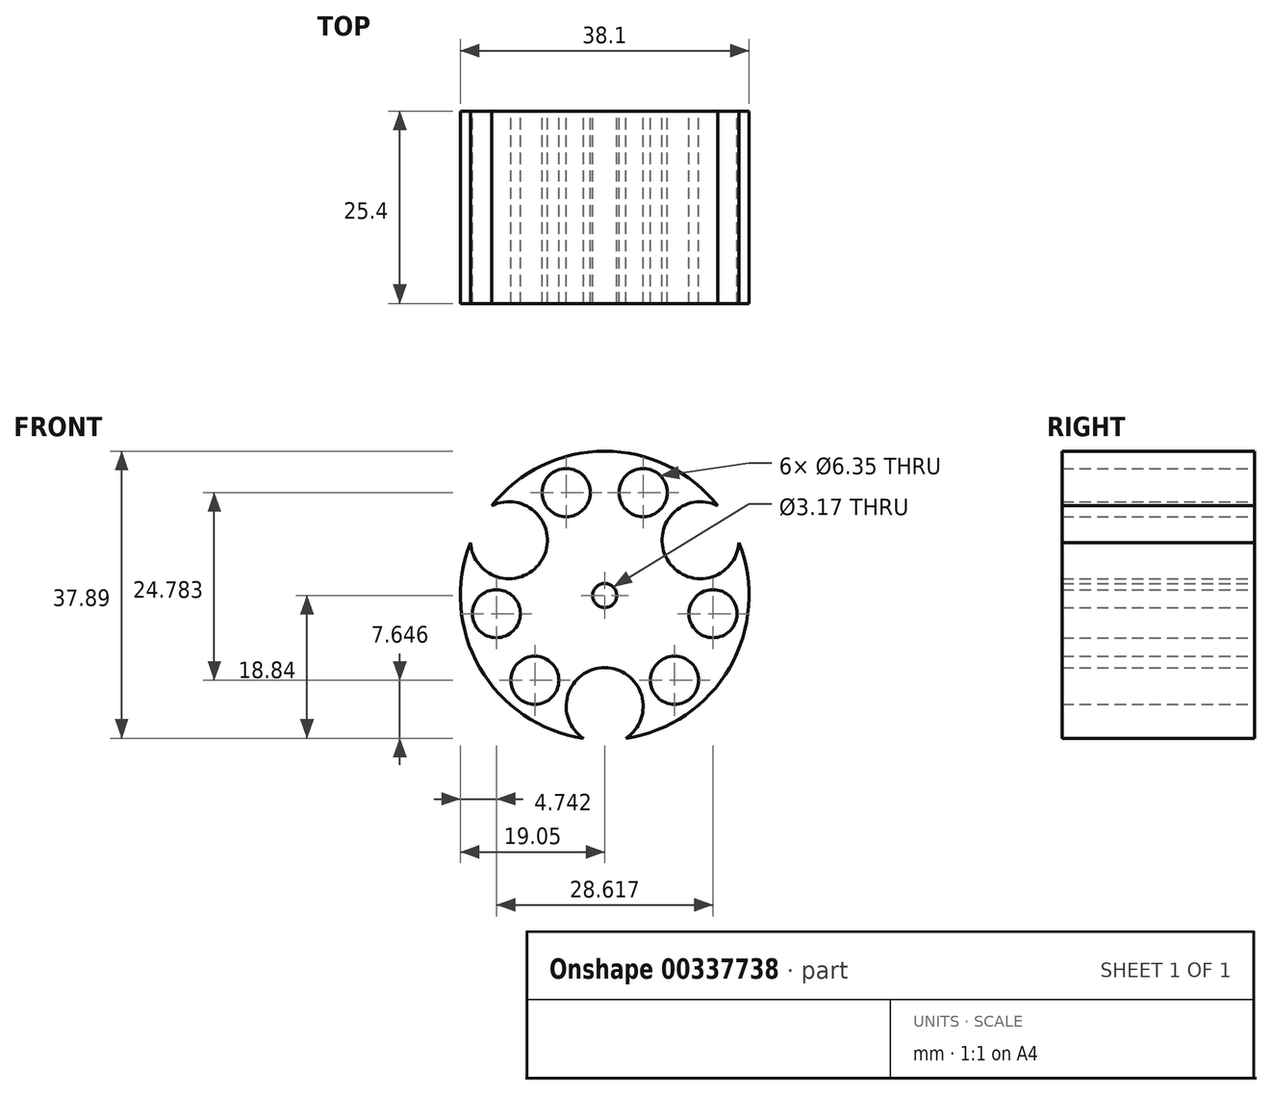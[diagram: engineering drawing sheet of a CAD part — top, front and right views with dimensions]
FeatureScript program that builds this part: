
annotation { "Feature Type Name" : "Feature", "Feature Type Description" : "" }
export const myFeature = defineFeature(function(context is Context, id is Id, definition is map)
    precondition{}
    {
        {
            var Q0;
            Q0=qCreatedBy(makeId("Front.planeOp"),FACE);
            var sketch = newSketch(context, id + "F0", { "sketchPlane" : qUnion([Q0])});
            skCircle(sketch, "E0", {"center": v(0, 0) * mm, "radius": 19.05 * mm, "construction": true});
            skCircle(sketch, "E1.cCircle", {"center": v(0, 0) * mm, "radius": 9.53 * mm, "construction": true});
            skPoint(sketch, "E2", {"position": v(0, -19.05) * mm});
            skPoint(sketch, "E3", {"position": v(-16.5, 9.53) * mm});
            skPoint(sketch, "E4", {"position": v(16.5, 9.52) * mm});
            skLineSegment(sketch, "E5", {"start": v(-16.5, 9.53) * mm, "end": v(0, -19.05) * mm, "construction": true});
            skLineSegment(sketch, "E6", {"start": v(16.5, 9.53) * mm, "end": v(0, -19.05) * mm, "construction": true});
            skArc(sketch, "E7", {"start": v(-17.72, 7) * mm, "mid": v(-16.5, -9.52) * mm, "end": v(-2.8, -18.84) * mm});
            skArc(sketch, "E8", {"start": v(2.8, -18.84) * mm, "mid": v(16.5, -9.53) * mm, "end": v(17.72, 7) * mm});
            skArc(sketch, "E9", {"start": v(14.92, 11.85) * mm, "mid": v(0, 19.05) * mm, "end": v(-14.92, 11.85) * mm});
            skArc(sketch, "E10", {"start": v(14.92, 11.85) * mm, "mid": v(8.25, 4.76) * mm, "end": v(17.72, 7) * mm});
            skArc(sketch, "E11", {"start": v(2.8, -18.84) * mm, "mid": v(0, -9.52) * mm, "end": v(-2.8, -18.84) * mm});
            skArc(sketch, "E12", {"start": v(-17.72, 7) * mm, "mid": v(-8.25, 4.76) * mm, "end": v(-14.92, 11.85) * mm});
            skCircle(sketch, "E13", {"center": v(0, 0) * mm, "radius": 1.59 * mm});
            skLineSegment(sketch, "E14", {"start": v(-16.5, 9.53) * mm, "end": v(16.5, 9.52) * mm, "construction": true});
            skCircle(sketch, "E15", {"center": v(-14.3, -2.4) * mm, "radius": 3.18 * mm});
            skCircle(sketch, "E16", {"center": v(14.3, -2.4) * mm, "radius": 3.18 * mm});
            skLineSegment(sketch, "E17", {"start": v(0, -19.05) * mm, "end": v(0, 19.05) * mm, "construction": true});
            skCircle(sketch, "E18", {"center": v(5.08, 13.59) * mm, "radius": 3.18 * mm});
            skCircle(sketch, "E19", {"center": v(-5.08, 13.59) * mm, "radius": 3.18 * mm});
            skCircle(sketch, "E20", {"center": v(9.23, -11.2) * mm, "radius": 3.18 * mm});
            skCircle(sketch, "E21", {"center": v(-9.23, -11.2) * mm, "radius": 3.18 * mm});
            skLineSegment(sketch, "E22", {"start": v(-16.5, 9.53) * mm, "end": v(16.5, -9.53) * mm, "construction": true});
            skLineSegment(sketch, "E23", {"start": v(16.5, 9.53) * mm, "end": v(-16.5, -9.53) * mm, "construction": true});
            skSolve(sketch);
        }
        {
            var Q0;
            Q0=makeQuery(id+"F0.imprint","IMPRINT",FACE,{"disambiguationData":[TD([[makeQuery(id+"F0.imprint","IMPRINT",EDGE,{"derivedFrom":sQuery(id+"F0.wireOp",EDGE,"E7")}),1.0]])]});
            extrude(context, id + "F1", {"entities" : qUnion([Q0]), "depth" : 25.4 * mm, "symmetric" : true});
        }
    });
